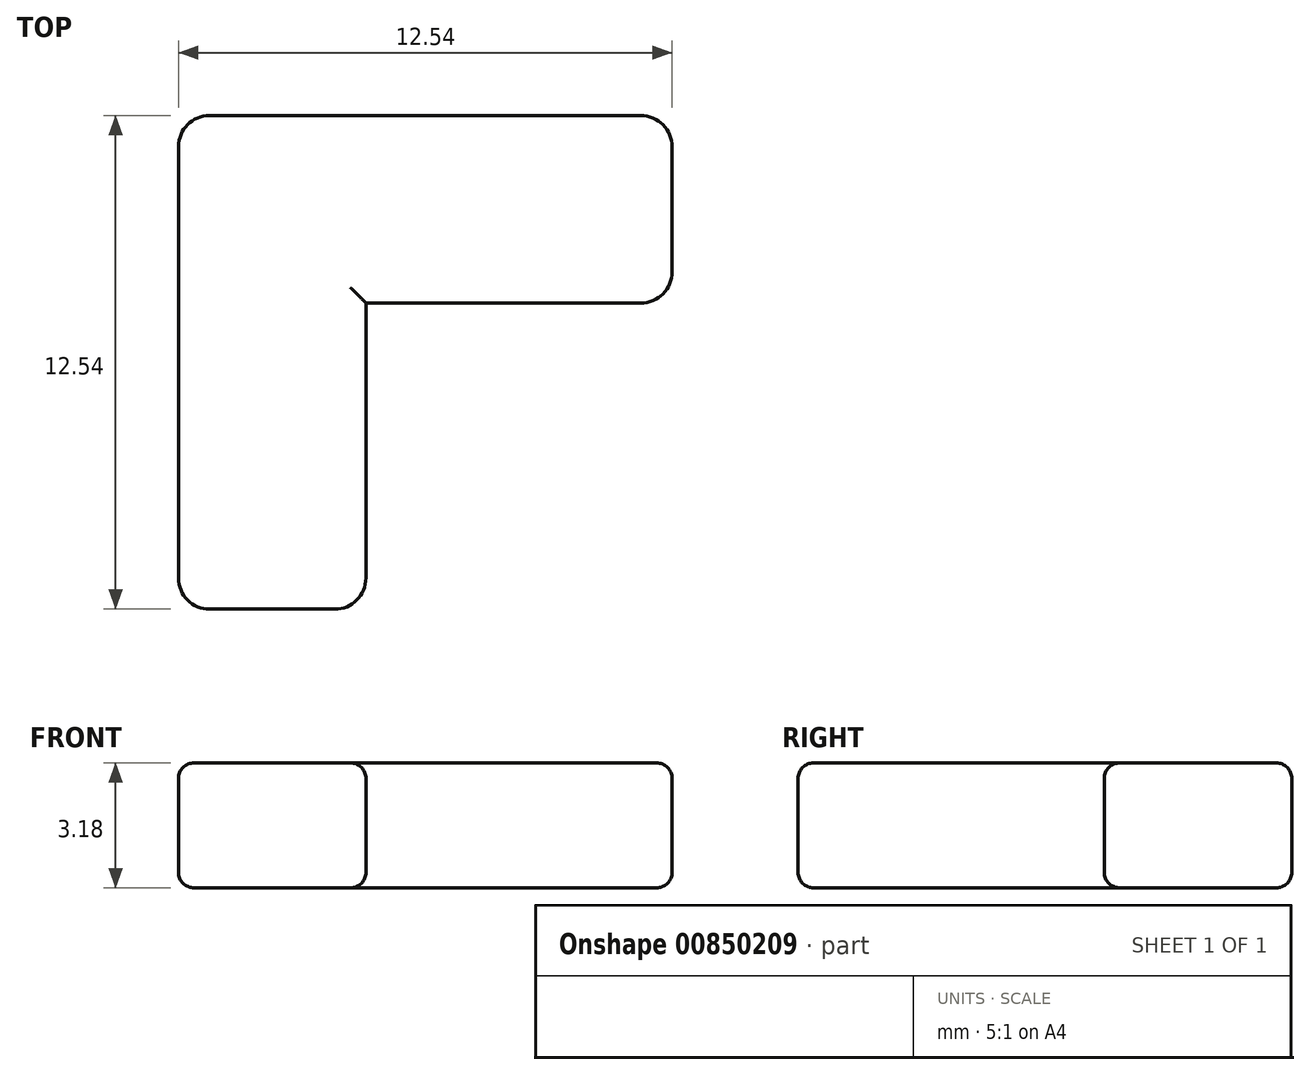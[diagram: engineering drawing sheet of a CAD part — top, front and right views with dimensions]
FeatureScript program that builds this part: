
annotation { "Feature Type Name" : "Feature", "Feature Type Description" : "" }
export const myFeature = defineFeature(function(context is Context, id is Id, definition is map)
    precondition{}
    {
        {
            var Q0;
            Q0=qCreatedBy(makeId("Top.planeOp"),FACE);
            var sketch = newSketch(context, id + "F0", { "sketchPlane" : qUnion([Q0])});
            skLineSegment(sketch, "E0.top", {"start": v(1.59, -10.16) * mm, "end": v(-1.59, -10.16) * mm});
            skLineSegment(sketch, "E0.left", {"start": v(2.38, 2.38) * mm, "end": v(2.38, -9.37) * mm});
            skLineSegment(sketch, "E0.right", {"start": v(-2.38, 1.6) * mm, "end": v(-2.38, -9.37) * mm});
            skPoint(sketch, "E0.middle", {"position": v(0, 0) * mm});
            skLineSegment(sketch, "E1.bottom", {"start": v(9.37, 2.38) * mm, "end": v(-1.6, 2.38) * mm});
            skLineSegment(sketch, "E1.top", {"start": v(9.37, -2.38) * mm, "end": v(-2.38, -2.38) * mm});
            skLineSegment(sketch, "E1.left", {"start": v(10.16, 1.59) * mm, "end": v(10.16, -1.59) * mm});
            skPoint(sketch, "E2.visualSharp", {"position": v(10.16, 2.38) * mm});
            skArc(sketch, "E2.filletArc", {"start": v(10.16, 1.59) * mm, "mid": v(9.93, 2.15) * mm, "end": v(9.37, 2.38) * mm});
            skPoint(sketch, "E3.visualSharp", {"position": v(10.16, -2.38) * mm});
            skArc(sketch, "E3.filletArc", {"start": v(9.37, -2.38) * mm, "mid": v(9.93, -2.15) * mm, "end": v(10.16, -1.59) * mm});
            skPoint(sketch, "E4.visualSharp", {"position": v(2.38, -10.16) * mm});
            skArc(sketch, "E4.filletArc", {"start": v(1.59, -10.16) * mm, "mid": v(2.15, -9.93) * mm, "end": v(2.38, -9.37) * mm});
            skPoint(sketch, "E5.visualSharp", {"position": v(-2.38, -10.16) * mm});
            skArc(sketch, "E5.filletArc", {"start": v(-2.38, -9.37) * mm, "mid": v(-2.15, -9.93) * mm, "end": v(-1.59, -10.16) * mm});
            skPoint(sketch, "E6.visualSharp", {"position": v(-2.38, 2.38) * mm});
            skArc(sketch, "E6.filletArc", {"start": v(-1.6, 2.38) * mm, "mid": v(-2.15, 2.15) * mm, "end": v(-2.38, 1.6) * mm});
            skSolve(sketch);
        }
        {
            var Q0;
            Q0 = qSketchRegion(id + "F0", true);
            extrude(context, id + "F1", {"entities" : qUnion([Q0]), "depth" : 3.17 * mm, "offsetDistance" : 25.4 * mm});
        }
        {
            var Q0;
            Q0=makeQuery(id+"F1.opExtrude","CAP_FACE",FACE,{"disambiguationData":[OSD([sQuery(id+"F0.wireOp",EDGE,"E0.bottom"),sQuery(id+"F0.wireOp",EDGE,"E0.top"),sQuery(id+"F0.wireOp",EDGE,"E0.left"),sQuery(id+"F0.wireOp",EDGE,"E0.right"),sQuery(id+"F0.wireOp",EDGE,"E1.bottom"),sQuery(id+"F0.wireOp",EDGE,"E1.top"),sQuery(id+"F0.wireOp",EDGE,"E1.left"),sQuery(id+"F0.wireOp",EDGE,"E1.right"),sQuery(id+"F0.wireOp",EDGE,"e48c8cea-de37-4d7b-bebe-fad5d6120350.filletArc"),sQuery(id+"F0.wireOp",EDGE,"ac0e0184-b8f9-40ee-be1f-0dbaa781b01f.filletArc"),sQuery(id+"F0.wireOp",EDGE,"E2.filletArc"),sQuery(id+"F0.wireOp",EDGE,"E3.filletArc"),sQuery(id+"F0.wireOp",EDGE,"E4.filletArc"),sQuery(id+"F0.wireOp",EDGE,"E5.filletArc"),sQuery(id+"F0.wireOp",EDGE,"ba0d1dea-405a-4f2e-90bb-12ae5f221d67.filletArc"),sQuery(id+"F0.wireOp",EDGE,"ddbfc01b-823f-4757-9cb3-bee3a7d0a760.filletArc")])],"isStart":false});
            var Q1;
            Q1=makeQuery(id+"F1.opExtrude","CAP_FACE",FACE,{"disambiguationData":[OSD([sQuery(id+"F0.wireOp",EDGE,"E0.bottom"),sQuery(id+"F0.wireOp",EDGE,"E0.top"),sQuery(id+"F0.wireOp",EDGE,"E0.left"),sQuery(id+"F0.wireOp",EDGE,"E0.right"),sQuery(id+"F0.wireOp",EDGE,"E1.bottom"),sQuery(id+"F0.wireOp",EDGE,"E1.top"),sQuery(id+"F0.wireOp",EDGE,"E1.left"),sQuery(id+"F0.wireOp",EDGE,"E1.right"),sQuery(id+"F0.wireOp",EDGE,"e48c8cea-de37-4d7b-bebe-fad5d6120350.filletArc"),sQuery(id+"F0.wireOp",EDGE,"ac0e0184-b8f9-40ee-be1f-0dbaa781b01f.filletArc"),sQuery(id+"F0.wireOp",EDGE,"E2.filletArc"),sQuery(id+"F0.wireOp",EDGE,"E3.filletArc"),sQuery(id+"F0.wireOp",EDGE,"E4.filletArc"),sQuery(id+"F0.wireOp",EDGE,"E5.filletArc"),sQuery(id+"F0.wireOp",EDGE,"ba0d1dea-405a-4f2e-90bb-12ae5f221d67.filletArc"),sQuery(id+"F0.wireOp",EDGE,"ddbfc01b-823f-4757-9cb3-bee3a7d0a760.filletArc")])],"isStart":true});
            fillet(context, id + "F2", {"entities" : qUnion([Q0, Q1]), "tangentPropagation" : true, "radius" : 0.4 * mm, "defaultsChanged" : false, "vertexSettings" : [], "allowEdgeOverflow" : false});
        }
    });
